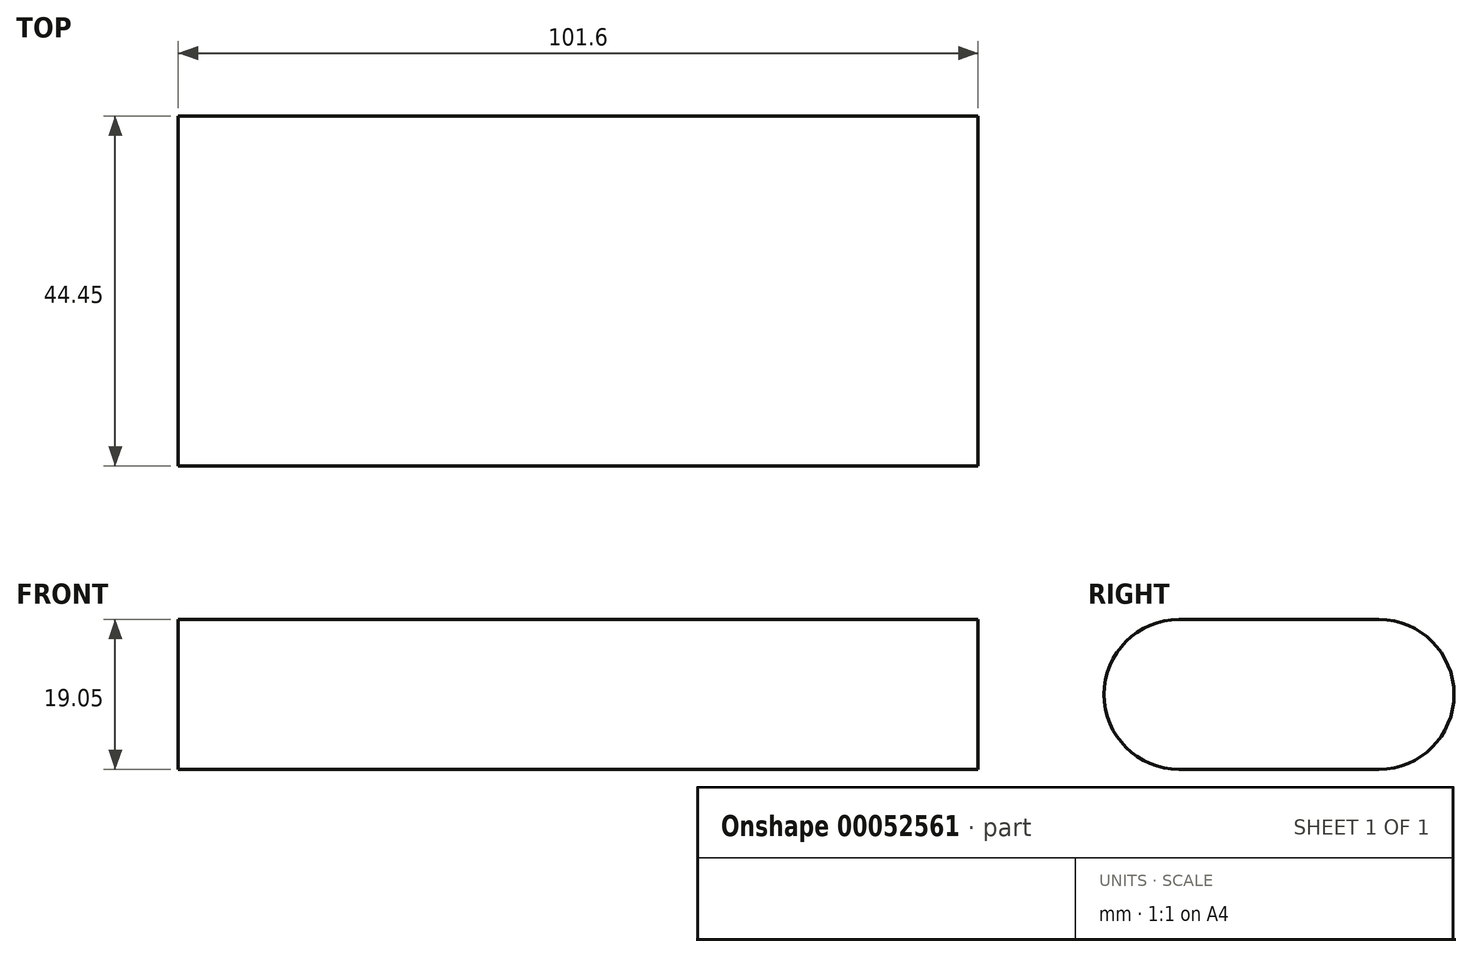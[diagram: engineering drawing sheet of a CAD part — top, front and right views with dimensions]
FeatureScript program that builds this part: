
annotation { "Feature Type Name" : "Feature", "Feature Type Description" : "" }
export const myFeature = defineFeature(function(context is Context, id is Id, definition is map)
    precondition{}
    {
        {
            var Q0;
            Q0=qCreatedBy(makeId("Right.planeOp"),FACE);
            var sketch = newSketch(context, id + "F0", { "sketchPlane" : qUnion([Q0])});
            skLineSegment(sketch, "E0.bottom", {"start": v(0, 0) * mm, "end": v(25.4, 0) * mm});
            skLineSegment(sketch, "E0.top", {"start": v(0, 19.05) * mm, "end": v(25.4, 19.05) * mm});
            skArc(sketch, "E1", {"start": v(0, 19.05) * mm, "mid": v(-9.53, 9.53) * mm, "end": v(0, 0) * mm});
            skArc(sketch, "E2", {"start": v(25.4, 0) * mm, "mid": v(34.93, 9.53) * mm, "end": v(25.4, 19.05) * mm});
            skSolve(sketch);
        }
        {
            var Q0;
            Q0=makeQuery(id+"F0.imprint","IMPRINT",FACE,{"disambiguationData":[TD([[makeQuery(id+"F0.imprint","IMPRINT",EDGE,{"derivedFrom":sQuery(id+"F0.wireOp",EDGE,"E0.bottom")}),1.0]])]});
            extrude(context, id + "F1", {"entities" : qUnion([Q0]), "depth" : 101.6 * mm});
        }
    });
